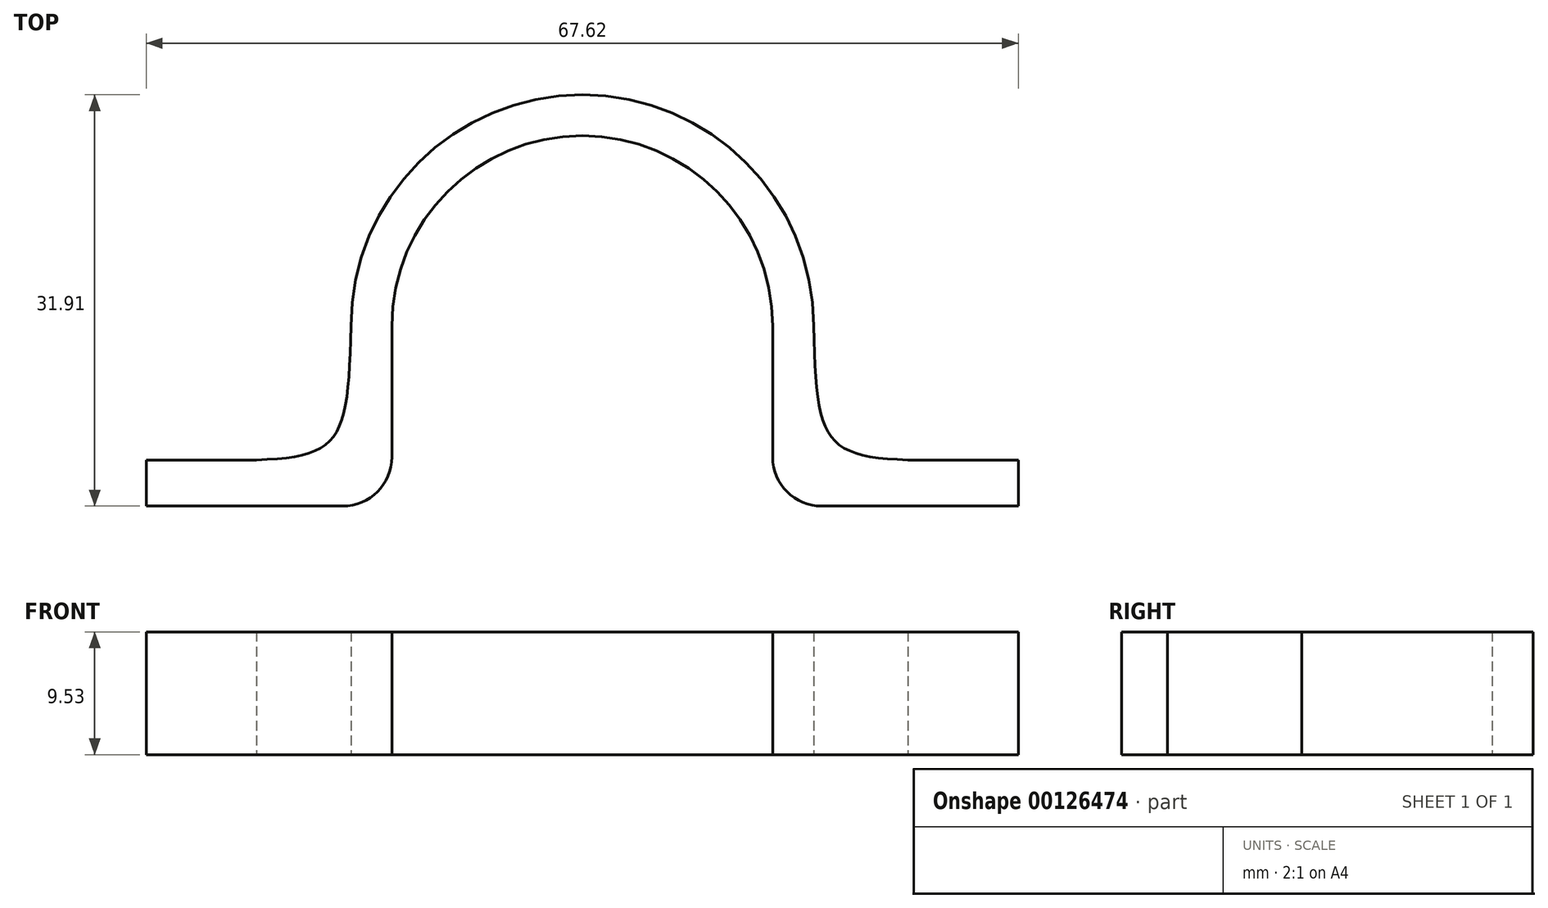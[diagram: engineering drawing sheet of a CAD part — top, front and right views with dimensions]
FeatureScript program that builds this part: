
annotation { "Feature Type Name" : "Feature", "Feature Type Description" : "" }
export const myFeature = defineFeature(function(context is Context, id is Id, definition is map)
    precondition{}
    {
        {
            var Q0;
            Q0=qCreatedBy(makeId("Top.planeOp"),FACE);
            var sketch = newSketch(context, id + "F0", { "sketchPlane" : qUnion([Q0])});
            skCircle(sketch, "E0", {"center": v(0, 0) * mm, "radius": 13.97 * mm, "construction": true});
            skCircle(sketch, "E1", {"center": v(0, 0) * mm, "radius": 14.76 * mm, "construction": true});
            skArc(sketch, "E2", {"start": v(14.76, 0) * mm, "mid": v(10.44, 10.44) * mm, "end": v(0, 14.76) * mm});
            skLineSegment(sketch, "E3", {"start": v(14.76, 0) * mm, "end": v(14.76, -10.16) * mm});
            skPoint(sketch, "E4", {"position": v(0, 14.76) * mm});
            skPoint(sketch, "E5", {"position": v(14.76, -13.97) * mm});
            skCircle(sketch, "E6", {"center": v(0, 0) * mm, "radius": 17.94 * mm, "construction": true});
            skLineSegment(sketch, "E7", {"start": v(18.57, -13.97) * mm, "end": v(33.81, -13.97) * mm});
            skArc(sketch, "E8.filletArc", {"start": v(14.76, -10.16) * mm, "mid": v(15.88, -12.85) * mm, "end": v(18.57, -13.97) * mm});
            skPoint(sketch, "E9", {"position": v(0, 17.94) * mm});
            skArc(sketch, "E10", {"start": v(17.94, 0) * mm, "mid": v(12.68, 12.68) * mm, "end": v(0, 17.94) * mm});
            skLineSegment(sketch, "E11", {"start": v(25.26, -10.39) * mm, "end": v(33.81, -10.39) * mm});
            skLineSegment(sketch, "E12", {"start": v(33.81, -10.39) * mm, "end": v(33.81, -13.97) * mm});
            skLineSegment(sketch, "E13", {"start": v(0, 0) * mm, "end": v(0, 17.94) * mm, "construction": true});
            skArc(sketch, "E14.MirrorCS", {"start": v(-17.94, 0) * mm, "mid": v(-12.68, 12.68) * mm, "end": v(0, 17.94) * mm});
            skArc(sketch, "E15.MirrorCS", {"start": v(-14.76, 0) * mm, "mid": v(-10.44, 10.44) * mm, "end": v(0, 14.76) * mm});
            skLineSegment(sketch, "E16.MirrorCS", {"start": v(-14.76, 0) * mm, "end": v(-14.76, -10.16) * mm});
            skLineSegment(sketch, "E17.MirrorCS", {"start": v(-25.26, -10.39) * mm, "end": v(-33.81, -10.39) * mm});
            skLineSegment(sketch, "E18.MirrorCS", {"start": v(-33.81, -10.39) * mm, "end": v(-33.81, -13.97) * mm});
            skLineSegment(sketch, "E19.MirrorCS", {"start": v(-18.57, -13.97) * mm, "end": v(-33.81, -13.97) * mm});
            skArc(sketch, "E20.MirrorCS", {"start": v(-14.76, -10.16) * mm, "mid": v(-15.88, -12.85) * mm, "end": v(-18.57, -13.97) * mm});
            skLineSegment(sketch, "E21", {"start": v(-17.94, 0) * mm, "end": v(17.94, 0) * mm, "construction": true});
            skLineSegment(sketch, "E22", {"start": v(0, 0) * mm, "end": v(0, -13.97) * mm, "construction": true});
            skFitSpline(sketch, "E23", {"points": [v(17.94, 0) * mm, v(25.26, -10.39) * mm], "startDerivative": vector(0.67, -26.3) * mm, "endDerivative": vector(20.07, -0.69) * mm});
            skFitSpline(sketch, "E24.MirrorCS", {"points": [v(-17.94, 0) * mm, v(-25.26, -10.39) * mm], "startDerivative": vector(-0.67, -26.3) * mm, "endDerivative": vector(-20.07, -0.69) * mm});
            skLineSegment(sketch, "E25", {"start": v(-33.81, -13.97) * mm, "end": v(39.37, -13.97) * mm, "construction": true});
            skSolve(sketch);
        }
        {
            var Q0;
            Q0 = qSketchRegion(id + "F0", true);
            var Q1;
            Q1=makeQuery(id+"F0.imprint","IMPRINT",FACE,{"disambiguationData":[TD([[makeQuery(id+"F0.imprint","IMPRINT",EDGE,{"derivedFrom":sQuery(id+"F0.wireOp",EDGE,"E2")}),-1.0]])]});
            extrude(context, id + "F1", {"entities" : qUnion([Q0, Q1]), "depth" : 9.52 * mm});
        }
    });
